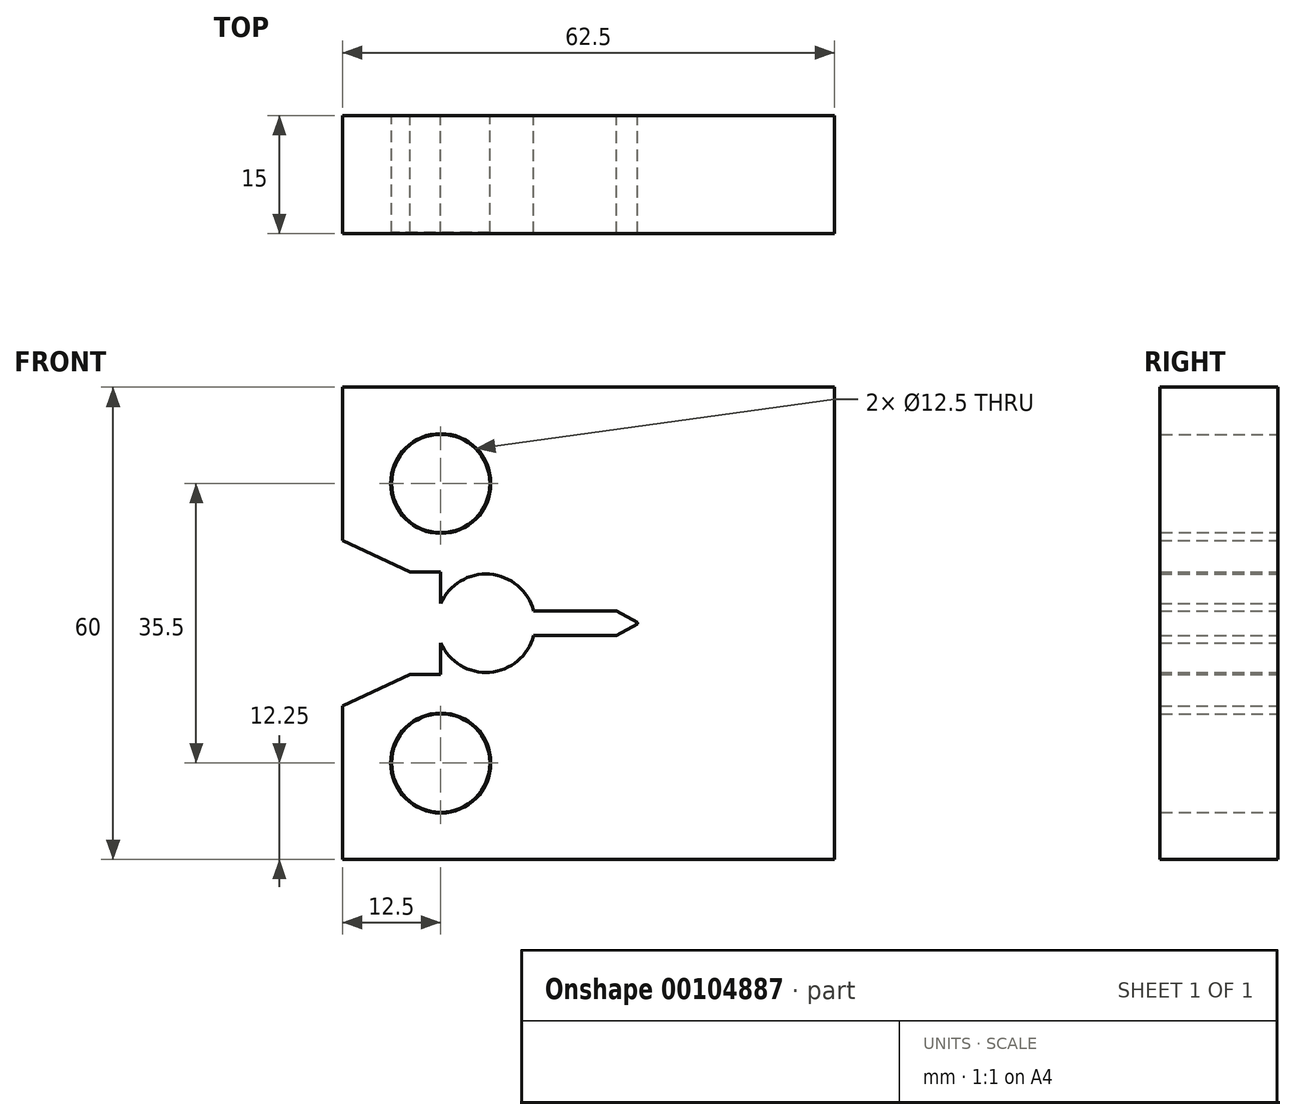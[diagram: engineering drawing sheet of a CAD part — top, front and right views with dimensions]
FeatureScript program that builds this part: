
annotation { "Feature Type Name" : "Feature", "Feature Type Description" : "" }
export const myFeature = defineFeature(function(context is Context, id is Id, definition is map)
    precondition{}
    {
        {
            var Q0;
            Q0=qCreatedBy(makeId("Front.planeOp"),FACE);
            var sketch = newSketch(context, id + "F0", { "sketchPlane" : qUnion([Q0])});
            skArc(sketch, "E0", {"start": v(0, 0) * mm, "mid": v(-0.01, 0.04) * mm, "end": v(-0.04, 0.07) * mm});
            skLineSegment(sketch, "E1", {"start": v(-2.65, 1.58) * mm, "end": v(-0.04, 0.07) * mm});
            skPoint(sketch, "E1.endSnap0", {"position": v(-0.04, 0.07) * mm});
            skLineSegment(sketch, "E2", {"start": v(-2.65, 1.58) * mm, "end": v(-13.22, 1.57) * mm});
            skLineSegment(sketch, "E3", {"start": v(-20, 1.57) * mm, "end": v(-20, 2.5) * mm, "construction": true});
            skLineSegment(sketch, "E4", {"start": v(-20, 2.5) * mm, "end": v(-22.39, 2.5) * mm, "construction": true});
            skLineSegment(sketch, "E5", {"start": v(-25, 2.5) * mm, "end": v(-25, 6.5) * mm});
            skLineSegment(sketch, "E6", {"start": v(-25, 6.5) * mm, "end": v(-28.92, 6.5) * mm});
            skLineSegment(sketch, "E7", {"start": v(-28.92, 6.5) * mm, "end": v(-37.5, 10.5) * mm});
            skLineSegment(sketch, "E8", {"start": v(-37.5, 10.5) * mm, "end": v(-37.5, 30) * mm});
            skLineSegment(sketch, "E9", {"start": v(-37.5, 30) * mm, "end": v(25, 30) * mm});
            skLineSegment(sketch, "E10", {"start": v(25, 30) * mm, "end": v(25, 0) * mm});
            skLineSegment(sketch, "E11", {"start": v(25, 0) * mm, "end": v(14.3, 0) * mm});
            skCircle(sketch, "E12", {"center": v(-25, 17.75) * mm, "radius": 6.25 * mm});
            skLineSegment(sketch, "E13", {"start": v(-25, 2.5) * mm, "end": v(-24.53, 3.5) * mm, "construction": true});
            skLineSegment(sketch, "E14", {"start": v(-24.53, 3.5) * mm, "end": v(-22.39, 2.5) * mm, "construction": true});
            skLineSegment(sketch, "E15", {"start": v(-13.22, 1.57) * mm, "end": v(-20, 1.57) * mm, "construction": true});
            skArc(sketch, "E16", {"start": v(-25, 2.5) * mm, "mid": v(-19.76, -6.23) * mm, "end": v(-13.22, 1.57) * mm, "construction": true});
            skArc(sketch, "E17", {"start": v(-13.22, 1.58) * mm, "mid": v(-18.78, 6.23) * mm, "end": v(-25, 2.5) * mm});
            skLineSegment(sketch, "E18", {"start": v(14.3, 0) * mm, "end": v(0, 0) * mm});
            skSolve(sketch);
        }
        {
            var Q0;
            Q0=makeQuery(id+"F0.imprint","IMPRINT",FACE,{"disambiguationData":[TD([[makeQuery(id+"F0.imprint","IMPRINT",EDGE,{"derivedFrom":sQuery(id+"F0.wireOp",EDGE,"E0")}),-1.0]])]});
            extrude(context, id + "F1", {"entities" : qUnion([Q0]), "depth" : 15 * mm, "symmetric" : true});
        }
        {
            var Q0;
            Q0=makeQuery(id+"F1.opExtrude","SWEPT_BODY",BODY,{"disambiguationData":[OSD([sQuery(id+"F0.wireOp",EDGE,"E0"),sQuery(id+"F0.wireOp",EDGE,"E1"),sQuery(id+"F0.wireOp",EDGE,"E2"),sQuery(id+"F0.wireOp",EDGE,"E3"),sQuery(id+"F0.wireOp",EDGE,"E4"),sQuery(id+"F0.wireOp",EDGE,"E5"),sQuery(id+"F0.wireOp",EDGE,"E6"),sQuery(id+"F0.wireOp",EDGE,"E7"),sQuery(id+"F0.wireOp",EDGE,"E8"),sQuery(id+"F0.wireOp",EDGE,"E9"),sQuery(id+"F0.wireOp",EDGE,"E10"),sQuery(id+"F0.wireOp",EDGE,"E11"),sQuery(id+"F0.wireOp",EDGE,"E12"),sQuery(id+"F0.wireOp",EDGE,"E13"),sQuery(id+"F0.wireOp",EDGE,"E14")])]});
            var Q1;
            Q1=makeQuery(id+"F1.opExtrude","SWEPT_FACE",FACE,{"disambiguationData":[OSD([sQuery(id+"F0.wireOp",EDGE,"E11")])]});
            mirror(context, id + "F2", {"operationType" : NewBodyOperationType.ADD, "entities" : qUnion([Q0]), "mirrorPlane" : qUnion([Q1])});
        }
        {
            var Q0;
            Q0=makeQuery(id+"F1.opExtrude","CAP_EDGE",EDGE,{"disambiguationData":[OSD([sQuery(id+"F0.wireOp",EDGE,"E12")])],"isStart":false});
            var Q1;
            Q1=makeQuery(id+"F2.opPattern","COPY",EDGE,{"derivedFrom":makeQuery(id+"F1.opExtrude","CAP_EDGE",EDGE,{"disambiguationData":[OSD([sQuery(id+"F0.wireOp",EDGE,"E12")])],"isStart":false}),"instanceName":"1"});
            var Q2;
            Q2=makeQuery(id+"F1.opExtrude","CAP_EDGE",EDGE,{"disambiguationData":[OSD([sQuery(id+"F0.wireOp",EDGE,"E12")])],"isStart":true});
            var Q3;
            Q3=makeQuery(id+"F2.opPattern","COPY",EDGE,{"derivedFrom":makeQuery(id+"F1.opExtrude","CAP_EDGE",EDGE,{"disambiguationData":[OSD([sQuery(id+"F0.wireOp",EDGE,"E12")])],"isStart":true}),"instanceName":"1"});
            chamfer(context, id + "F3", {"entities" : qUnion([Q0, Q1, Q2, Q3]), "width" : 0.1 * mm, "tangentPropagation" : true});
        }
    });
